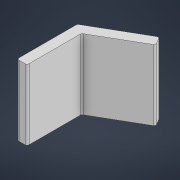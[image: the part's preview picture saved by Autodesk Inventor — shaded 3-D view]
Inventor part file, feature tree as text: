
AUTODESK INVENTOR PART (.ipt)
format: ipt  version: 2022 (Build 260153000, 153)  size: 123,904 bytes
history: native  units: mm
features: sketch x2, other x1, extrude x1, fillet x1, hole x1
ambient origin geometry x8: Origin, YZ Plane, XZ Plane, XY Plane, X Axis, Y Axis, Z Axis, Center Point
bodies: Body1 (feature_tree)
feature tree (6):
  other  "Твердое тело1"
  extrude  "Выдавливание1"  Depth=70.0mm TaperAngle=0.0deg
  fillet  "Сопряжение1"  Radius=60.0mm
  hole  "Отверстие1"  [1 undecoded]
  sketch  "Эскиз1"
  sketch  "Эскиз7"
note: 1 required parameter value undecoded (feature->parameter linkage not recoverable at this tier; creation-order binding heuristic only, values carry confidence <= 0.55)
